# Revit family: Hager-Vector-IP55-syst-SE-en
name_source: partatom
category: Electrical Equipment
units: mm (PartAtom-declared; Revit-internal decimal feet)

## family parameters
Cut with Voids When Loaded = No
Host = Face
Panel Configuration = Two Columns, Circuits Across
Part Type = Panelboard
Room Calculation Point = No
Round Connector Dimension = Use Diameter
Shared = No

## types (9) — shared parameters
EF000003 - Mounting method = EV000384 - Surface mounted (plaster)
EF000007 - Colour = EV000270 - Grey
EF000116 - RAL-number = 7035
EF000118 - With mounting plate = No
EF000339 - Type of cover = EV004216 - Door
EF001062 - EMC-version = No
EF001088 - Extension possible = Yes
EF001134 - DIN-rail = Yes
EF001596 - Material housing = EV000139 - Plastic
EF004462 - Type of closure = EV000154 - Other
EF005474 - Degree of protection (IP) = EV006421 - IP65
EF006306 - With lock = No
EF009212 - Cover model = EV000116 - Closed
EF015776 - Earthing terminal block = No
EF015777 - Neutral terminal block = No
EF015941 - Signal passing door = Yes
HG000001 - Number of columns = 1
HG000002 - With door or cover = Yes
HG000003 - Range = Vector
HG000005 - Thickness = 3 mm  [stored 0.00984252 ft]
HG000006 - Flush mounted = No
HG000009 - Double swing door = No
HG000010 - Asymmetric doors = No
HG000011 - Empty rows from bottom = No
HG000017 - Distance between poles = 18 mm  [stored 0.0590551 ft]
Manufacturer = Hager
Type Comments = Vector
zero-valued in all types: Default Elevation, EF000218 - Built-in depth, EF000332 - Built-in height, EF000846 - Built-in width, HG000007 - Number of empty columns, HG000008 - Number of empty rows

## per-type parameters (varying)
| type | EF000008 - Width | EF000040 - Height | EF000049 - Depth | EF000266 - Number of rows | EF001131 - Internal depth | EF002950 - Width in number of modular spacings | EF006244 - Transparent cover/door | HG000004 - Manufacturer reference | Model |
| Surface mounted IP65 W111 H175 D93 3 Modular spacings - VE103S | 111 mm | 175 mm | 93 mm | 1 | 93 mm | 3 | Yes | VE103S | VE103S |
| Surface mounted IP65 W165 H190 D113 6 Modular spacings - VE106S | 165 mm | 190 mm | 113 mm | 1 | 113 mm | 6 | Yes | VE106S | VE106S |
| Surface mounted IP65 W310 H302 D151 12 Modular spacings - VE112S | 310 mm | 302 mm | 151 mm  [stored 0.495407 ft] | 1 | 151 mm  [stored 0.495407 ft] | 12 | No | VE112S | VE112S |
| Surface mounted IP65 W310 H427 D151 12 Modular spacings - VE212S | 310 mm | 427 mm | 151 mm  [stored 0.495407 ft] | 2 | 151 mm  [stored 0.495407 ft] | 12 | No | VE212S | VE212S |
| Surface mounted IP65 W310 H552 D151 12 Modular spacings - VE312S | 310 mm | 552 mm | 151 mm  [stored 0.495407 ft] | 3 | 151 mm  [stored 0.495407 ft] | 12 | No | VE312S | VE312S |
| Surface mounted IP65 W310 H677 D151 12 Modular spacings - VE412S | 310 mm | 677 mm | 151 mm  [stored 0.495407 ft] | 4 | 151 mm  [stored 0.495407 ft] | 12 | No | VE412S | VE412S |
| Surface mounted IP65 W418 H302 D151 18 Modular spacings - VE118S | 418 mm  [stored 1.37139 ft] | 302 mm | 151 mm  [stored 0.495407 ft] | 1 | 151 mm  [stored 0.495407 ft] | 18 | No | VE118S | VE118S |
| Surface mounted IP65 W418 H452 D151 18 Modular spacings - VE218S | 418 mm  [stored 1.37139 ft] | 452 mm | 151 mm  [stored 0.495407 ft] | 2 | 151 mm  [stored 0.495407 ft] | 18 | No | VE218S | VE218S |
| Surface mounted IP65 W418 H602 D151 18 Modular spacings - VE318S | 418 mm  [stored 1.37139 ft] | 602 mm  [stored 1.97507 ft] | 151 mm  [stored 0.495407 ft] | 3 | 151 mm  [stored 0.495407 ft] | 18 | No | VE318S | VE318S |

note: [stored X ft] marks values corroborated as IEEE doubles in the binary element streams (Revit-internal decimal feet)

## geometry (parser evidence)
native form markers: Sweep x17
no freeform markers — native parametric forms only
